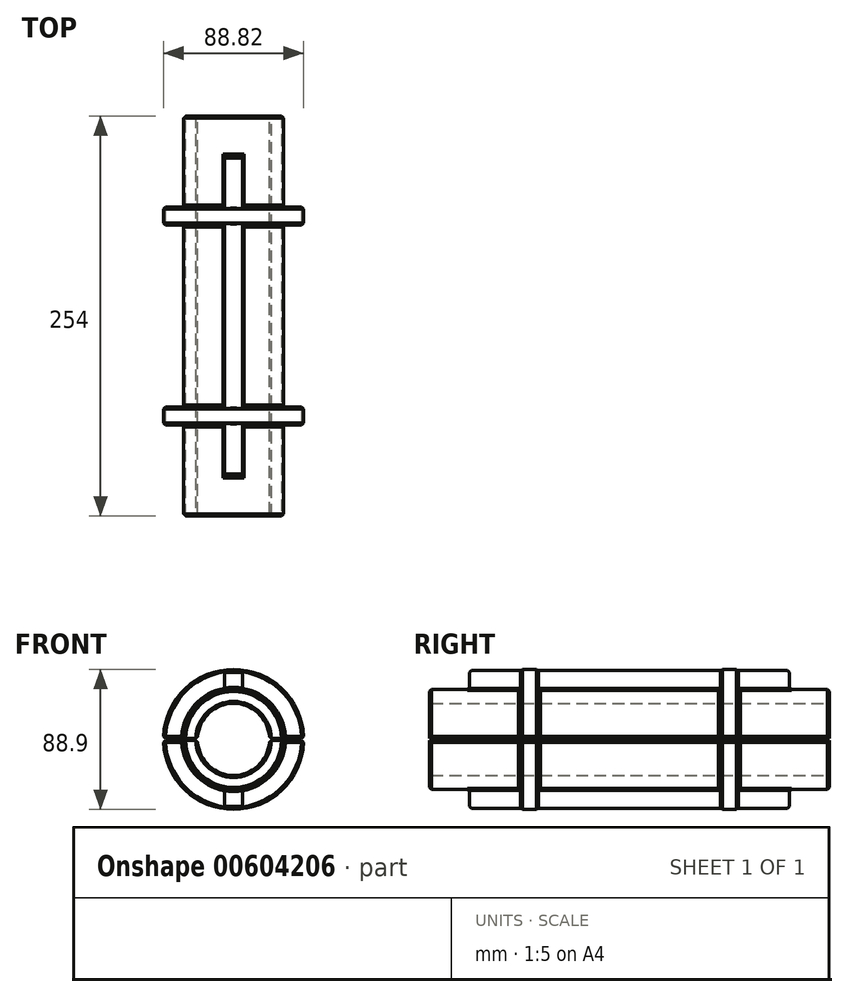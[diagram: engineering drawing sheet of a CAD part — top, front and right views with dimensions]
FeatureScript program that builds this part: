
annotation { "Feature Type Name" : "Feature", "Feature Type Description" : "" }
export const myFeature = defineFeature(function(context is Context, id is Id, definition is map)
    precondition{}
    {
        {
            var Q0;
            Q0=qCreatedBy(makeId("Top.planeOp"),FACE);
            var sketch = newSketch(context, id + "F0", { "sketchPlane" : qUnion([Q0])});
            skLineSegment(sketch, "E0", {"start": v(0, 0) * mm, "end": v(0, 254) * mm, "construction": true});
            skLineSegment(sketch, "E1", {"start": v(0, 254) * mm, "end": v(22.86, 254) * mm, "construction": true});
            skLineSegment(sketch, "E2", {"start": v(0, 0) * mm, "end": v(31.75, 0) * mm, "construction": true});
            skLineSegment(sketch, "E3", {"start": v(31.75, 0) * mm, "end": v(31.75, 57.79) * mm});
            skLineSegment(sketch, "E4", {"start": v(31.75, 57.79) * mm, "end": v(44.45, 57.79) * mm});
            skLineSegment(sketch, "E5", {"start": v(44.45, 57.79) * mm, "end": v(44.45, 69.22) * mm});
            skLineSegment(sketch, "E6", {"start": v(44.45, 69.22) * mm, "end": v(31.75, 69.22) * mm});
            skLineSegment(sketch, "E7", {"start": v(31.75, 69.22) * mm, "end": v(31.75, 184.78) * mm});
            skLineSegment(sketch, "E8", {"start": v(31.75, 254) * mm, "end": v(22.86, 254) * mm});
            skLineSegment(sketch, "E9", {"start": v(22.86, 0) * mm, "end": v(31.75, 0) * mm});
            skLineSegment(sketch, "E10", {"start": v(22.86, 0) * mm, "end": v(22.86, 254) * mm});
            skLineSegment(sketch, "E11", {"start": v(0, 127) * mm, "end": v(31.75, 127) * mm, "construction": true});
            skPoint(sketch, "E11.endSnap0", {"position": v(22.86, 127) * mm});
            skLineSegment(sketch, "E12.MirrorCS", {"start": v(44.45, 184.78) * mm, "end": v(31.75, 184.78) * mm});
            skLineSegment(sketch, "E13.MirrorCS", {"start": v(31.75, 196.22) * mm, "end": v(44.45, 196.22) * mm});
            skLineSegment(sketch, "E14.MirrorCS", {"start": v(44.45, 196.22) * mm, "end": v(44.45, 184.78) * mm});
            skLineSegment(sketch, "E15.trimOffspring", {"start": v(31.75, 196.22) * mm, "end": v(31.75, 254) * mm});
            skSolve(sketch);
        }
        {
            var Q0;
            Q0=makeQuery(id+"F0.imprint","IMPRINT",FACE,{"disambiguationData":[TD([[makeQuery(id+"F0.imprint","IMPRINT",EDGE,{"derivedFrom":sQuery(id+"F0.wireOp",EDGE,"E3")}),1.0]])]});
            var Q1;
            Q1=sQuery(id+"F0.wireOp",EDGE,"E0");
            revolve(context, id + "F1", {"entities" : qUnion([Q0]), "axis" : qUnion([Q1]), "revolveType" : RevolveType.ONE_DIRECTION, "oppositeDirection" : true, "angle" : 180 * degree});
        }
        {
            var Q0;
            Q0=makeQuery(id+"F1.opRevolve","SWEPT_FACE",FACE,{"disambiguationData":[OSD([sQuery(id+"F0.wireOp",EDGE,"E9")])]});
            cPlane(context, id + "F2", {"entities" : qUnion([Q0]), "cplaneType" : CPlaneType.OFFSET, "offset" : 25.4 * mm, "oppositeDirection" : true, "width" : 152.4 * mm, "height" : 152.4 * mm});
        }
        {
            var Q0;
            Q0=qCreatedBy(id+"F2.planeOp",FACE);
            var sketch = newSketch(context, id + "F3", { "sketchPlane" : qUnion([Q0])});
            skLineSegment(sketch, "E16", {"start": v(0, 0) * mm, "end": v(0, 43.93) * mm, "construction": true});
            skLineSegment(sketch, "E17", {"start": v(-5.71, 43.93) * mm, "end": v(-5.71, 31.23) * mm});
            skLineSegment(sketch, "E18", {"start": v(-5.71, 31.23) * mm, "end": v(5.71, 31.23) * mm});
            skLineSegment(sketch, "E19", {"start": v(5.72, 31.23) * mm, "end": v(5.72, 43.93) * mm});
            skLineSegment(sketch, "E20", {"start": v(5.71, 43.93) * mm, "end": v(-5.71, 43.93) * mm});
            skSolve(sketch);
        }
        {
            var Q0;
            Q0 = qSketchRegion(id + "F3", true);
            extrude(context, id + "F4", {"entities" : qUnion([Q0]), "operationType" : NewBodyOperationType.ADD, "oppositeDirection" : true, "depth" : 203.2 * mm, "offsetDistance" : 25.4 * mm});
        }
        {
            var Q0;
            Q0=qCreatedBy(makeId("Front.planeOp"),FACE);
            var sketch = newSketch(context, id + "F5", { "sketchPlane" : qUnion([Q0])});
            skLineSegment(sketch, "E21", {"start": v(-76.2, 0) * mm, "end": v(76.2, 0) * mm});
            skLineSegment(sketch, "E22", {"start": v(-76.2, 0) * mm, "end": v(-76.2, 0.63) * mm});
            skLineSegment(sketch, "E23", {"start": v(-76.2, 0.63) * mm, "end": v(76.2, 0.63) * mm});
            skLineSegment(sketch, "E24", {"start": v(76.2, 0.63) * mm, "end": v(76.2, 0) * mm});
            skSolve(sketch);
        }
        {
            var Q0;
            Q0 = qSketchRegion(id + "F5", true);
            extrude(context, id + "F6", {"entities" : qUnion([Q0]), "operationType" : NewBodyOperationType.REMOVE, "endBound" : BoundingType.THROUGH_ALL, "oppositeDirection" : true, "depth" : 25.4 * mm, "offsetDistance" : 25.4 * mm});
        }
        {
            var Q0;
            Q0=makeQuery(id+"F1.opRevolve","SWEPT_FACE",FACE,{"disambiguationData":[OSD([sQuery(id+"F0.wireOp",EDGE,"E3")])]});
            var Q1;
            {var subQ1=sQuery(id+"F0.wireOp",EDGE,"E7");Q1=makeQuery(id+"F4.boolean.opBoolean","SPLIT",FACE,{"disambiguationData":[TD([makeQuery(id+"F4.opExtrude","SWEPT_FACE",FACE,{"disambiguationData":[OSD([sQuery(id+"F3.wireOp",EDGE,"E19")])]})])],"derivedFrom":makeQuery(id+"F1.opRevolve","SWEPT_FACE",FACE,{"disambiguationData":[OSD([subQ1])]})});}
            var Q2;
            {var subQ1=sQuery(id+"F0.wireOp",EDGE,"E7");Q2=makeQuery(id+"F4.boolean.opBoolean","SPLIT",FACE,{"disambiguationData":[TD([makeQuery(id+"F4.opExtrude","SWEPT_FACE",FACE,{"disambiguationData":[OSD([sQuery(id+"F3.wireOp",EDGE,"E17")])]})])],"derivedFrom":makeQuery(id+"F1.opRevolve","SWEPT_FACE",FACE,{"disambiguationData":[OSD([subQ1])]})});}
            var Q3;
            Q3=makeQuery(id+"F1.opRevolve","SWEPT_FACE",FACE,{"disambiguationData":[OSD([sQuery(id+"F0.wireOp",EDGE,"E15.trimOffspring")])]});
            var Q4;
            Q4=makeQuery(id+"F1.opRevolve","SWEPT_FACE",FACE,{"disambiguationData":[OSD([sQuery(id+"F0.wireOp",EDGE,"E14.MirrorCS")])]});
            var Q5;
            Q5=makeQuery(id+"F1.opRevolve","SWEPT_FACE",FACE,{"disambiguationData":[OSD([sQuery(id+"F0.wireOp",EDGE,"E5")])]});
            var Q6;
            Q6=makeQuery(id+"F4.opExtrude","CAP_EDGE",EDGE,{"disambiguationData":[OSD([sQuery(id+"F3.wireOp",EDGE,"E20")])],"isStart":true});
            var Q7;
            Q7=makeQuery(id+"F4.opExtrude","CAP_EDGE",EDGE,{"disambiguationData":[OSD([sQuery(id+"F3.wireOp",EDGE,"E20")])],"isStart":false});
            var Q8;
            Q8=makeQuery(id+"F1.opRevolve","SWEPT_FACE",FACE,{"disambiguationData":[OSD([sQuery(id+"F0.wireOp",EDGE,"E10")])]});
            chamfer(context, id + "F7", {"entities" : qUnion([Q0, Q1, Q2, Q3, Q4, Q5, Q6, Q7, Q8]), "width" : 1.27 * mm, "tangentPropagation" : true});
        }
        {
            var Q0;
            Q0=makeQuery(id+"F1.opRevolve","SWEPT_BODY",BODY,{"disambiguationData":[OSD([sQuery(id+"F0.wireOp",EDGE,"E3"),sQuery(id+"F0.wireOp",EDGE,"E4"),sQuery(id+"F0.wireOp",EDGE,"E5"),sQuery(id+"F0.wireOp",EDGE,"E6"),sQuery(id+"F0.wireOp",EDGE,"E7"),sQuery(id+"F0.wireOp",EDGE,"E8"),sQuery(id+"F0.wireOp",EDGE,"E9"),sQuery(id+"F0.wireOp",EDGE,"E10"),sQuery(id+"F0.wireOp",EDGE,"E12.MirrorCS"),sQuery(id+"F0.wireOp",EDGE,"E13.MirrorCS"),sQuery(id+"F0.wireOp",EDGE,"E14.MirrorCS"),sQuery(id+"F0.wireOp",EDGE,"E15.trimOffspring")])]});
            var Q1;
            Q1=qCreatedBy(makeId("Top.planeOp"),FACE);
            mirror(context, id + "F8", {"entities" : qUnion([Q0]), "mirrorPlane" : qUnion([Q1])});
        }
    });
